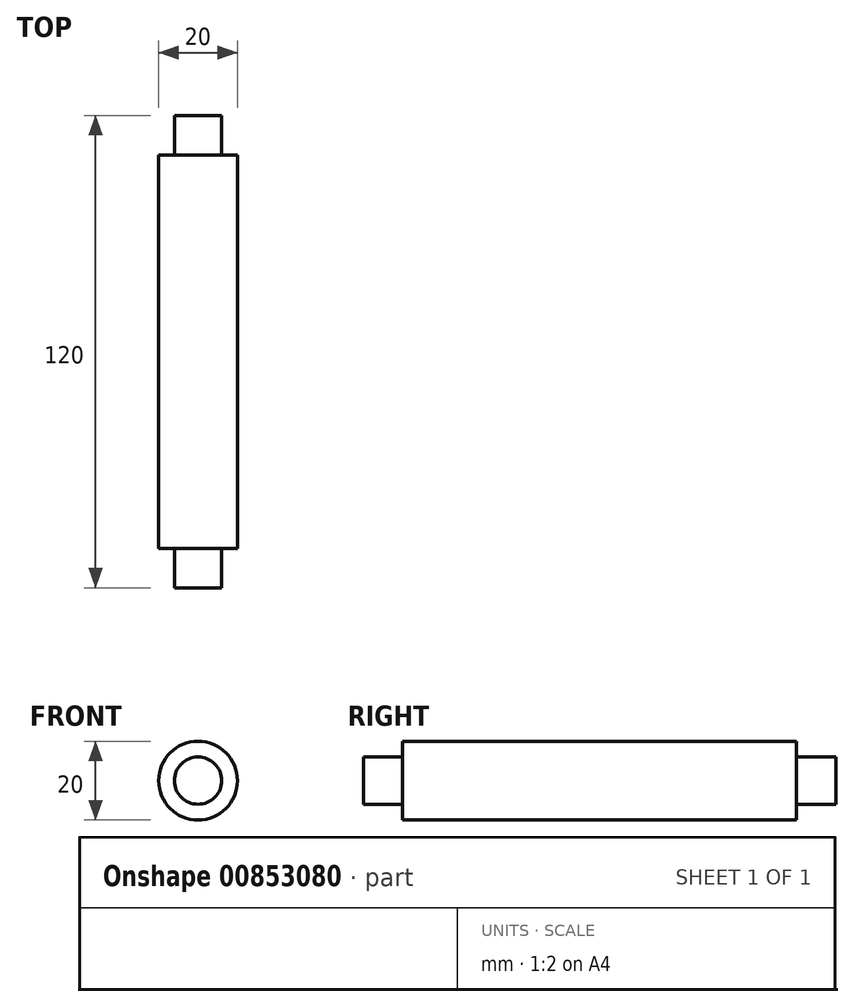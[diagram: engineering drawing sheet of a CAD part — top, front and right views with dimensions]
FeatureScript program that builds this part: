
annotation { "Feature Type Name" : "Feature", "Feature Type Description" : "" }
export const myFeature = defineFeature(function(context is Context, id is Id, definition is map)
    precondition{}
    {
        {
            var Q0;
            Q0=qCreatedBy(makeId("Top.planeOp"),FACE);
            var sketch = newSketch(context, id + "F0", { "sketchPlane" : qUnion([Q0])});
            skLineSegment(sketch, "E0.bottom", {"start": v(0, 0) * mm, "end": v(10, 0) * mm});
            skLineSegment(sketch, "E0.top", {"start": v(0, 100) * mm, "end": v(10, 100) * mm});
            skLineSegment(sketch, "E0.left", {"start": v(0, 0) * mm, "end": v(0, 100) * mm});
            skLineSegment(sketch, "E0.right", {"start": v(10, 0) * mm, "end": v(10, 100) * mm});
            skSolve(sketch);
        }
        {
            var Q0;
            Q0=makeQuery(id+"F0.imprint","IMPRINT",FACE,{"disambiguationData":[TD([[makeQuery(id+"F0.imprint","IMPRINT",EDGE,{"derivedFrom":sQuery(id+"F0.wireOp",EDGE,"E0.bottom")}),1.0]])]});
            var Q1;
            Q1=sQuery(id+"F0.wireOp",EDGE,"E0.left");
            revolve(context, id + "F1", {"surfaceOperationType" : NewSurfaceOperationType.NEW, "entities" : qUnion([Q0]), "axis" : qUnion([Q1]), "revolveType" : RevolveType.FULL});
        }
        {
            var Q0;
            Q0=qCreatedBy(makeId("Front.planeOp"),FACE);
            var sketch = newSketch(context, id + "F2", { "sketchPlane" : qUnion([Q0])});
            skCircle(sketch, "E1", {"center": v(0, 0) * mm, "radius": 6 * mm});
            skSolve(sketch);
        }
        {
            var Q0;
            Q0=makeQuery(id+"F2.imprint","IMPRINT",FACE,{"disambiguationData":[TD([[makeQuery(id+"F2.imprint","IMPRINT",EDGE,{"derivedFrom":sQuery(id+"F2.wireOp",EDGE,"E1")}),1.0]])]});
            extrude(context, id + "F3", {"entities" : qUnion([Q0]), "operationType" : NewBodyOperationType.ADD, "depth" : 10 * mm, "offsetDistance" : 25 * mm});
        }
        {
            var Q0;
            Q0=makeQuery(id+"F1.opRevolve","SWEPT_FACE",FACE,{"disambiguationData":[OSD([sQuery(id+"F0.wireOp",EDGE,"E0.top")])]});
            var sketch = newSketch(context, id + "F4", { "sketchPlane" : qUnion([Q0])});
            skCircle(sketch, "E2", {"center": v(0, 0) * mm, "radius": 6 * mm});
            skSolve(sketch);
        }
        {
            var Q0;
            Q0=makeQuery(id+"F4.imprint","IMPRINT",FACE,{"disambiguationData":[TD([[makeQuery(id+"F4.imprint","IMPRINT",EDGE,{"derivedFrom":sQuery(id+"F4.wireOp",EDGE,"E2")}),1.0]])]});
            var Q1;
            Q1=sQuery(id+"F4.wireOp",EDGE,"E2");
            extrude(context, id + "F5", {"entities" : qUnion([Q0]), "surfaceEntities" : qUnion([Q1]), "depth" : 10 * mm, "offsetDistance" : 25 * mm});
        }
    });
